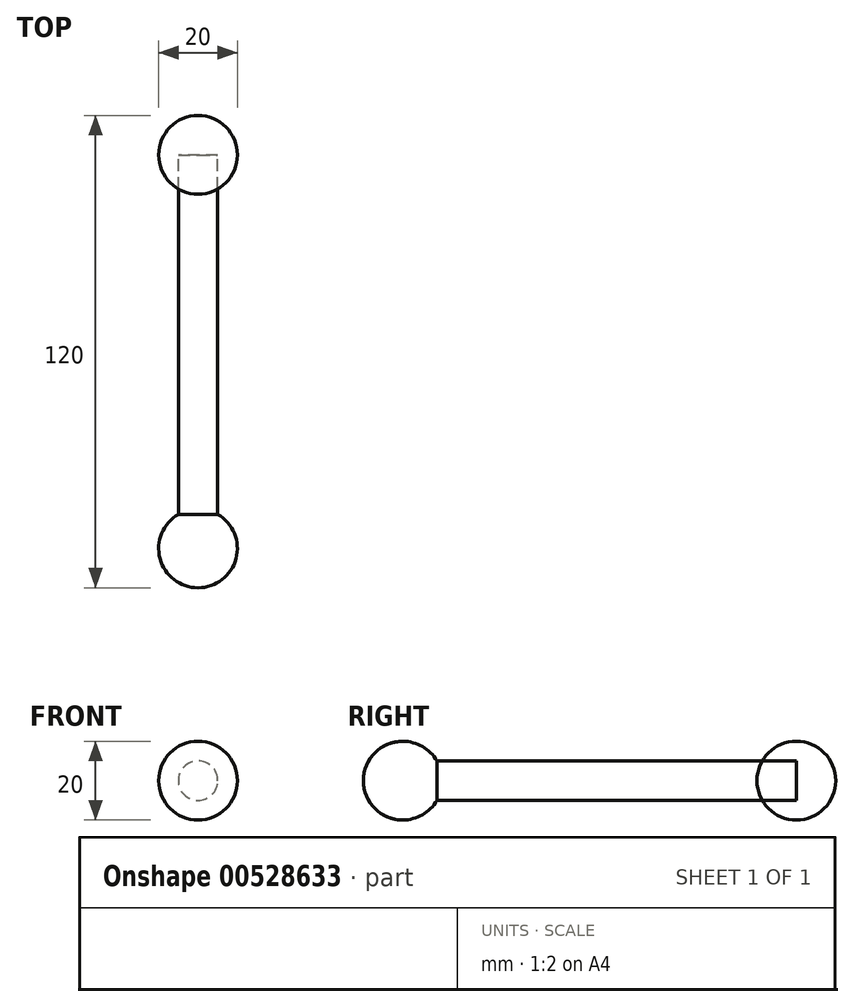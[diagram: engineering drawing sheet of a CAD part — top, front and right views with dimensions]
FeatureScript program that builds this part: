
annotation { "Feature Type Name" : "Feature", "Feature Type Description" : "" }
export const myFeature = defineFeature(function(context is Context, id is Id, definition is map)
    precondition{}
    {
        {
            var Q0;
            Q0=qCreatedBy(makeId("Front.planeOp"),FACE);
            var sketch = newSketch(context, id + "F0", { "sketchPlane" : qUnion([Q0])});
            skCircle(sketch, "E0", {"center": v(0, 0) * mm, "radius": 5 * mm});
            skSolve(sketch);
        }
        {
            var Q0;
            Q0 = qSketchRegion(id + "F0", true);
            extrude(context, id + "F1", {"entities" : qUnion([Q0]), "depth" : 100 * mm, "offsetDistance" : 25 * mm});
        }
        {
            var Q0;
            Q0=qCreatedBy(makeId("Right.planeOp"),FACE);
            var sketch = newSketch(context, id + "F2", { "sketchPlane" : qUnion([Q0])});
            skLineSegment(sketch, "E1", {"start": v(0, 10) * mm, "end": v(0, -10) * mm});
            skArc(sketch, "E2", {"start": v(0, 10) * mm, "mid": v(-10, 0) * mm, "end": v(0, -10) * mm});
            skLineSegment(sketch, "E3", {"start": v(-8.66, -5) * mm, "end": v(-91.34, -5) * mm});
            skLineSegment(sketch, "E4", {"start": v(-91.34, 5) * mm, "end": v(-8.66, 5) * mm});
            skLineSegment(sketch, "E5", {"start": v(-50, 5) * mm, "end": v(-50, -10) * mm, "construction": true});
            skArc(sketch, "E6.MirrorCS", {"start": v(-100, 10) * mm, "mid": v(-90, 0) * mm, "end": v(-100, -10) * mm});
            skLineSegment(sketch, "E7.MirrorCS", {"start": v(-100, 10) * mm, "end": v(-100, -10) * mm});
            skPoint(sketch, "E8.orphan", {"position": v(0, 5) * mm});
            skPoint(sketch, "E9.orphan", {"position": v(-100, 5) * mm});
            skSolve(sketch);
        }
        {
            var Q0;
            {var subQ0=sQuery(id+"F2.wireOp",EDGE,"E1");Q0=makeQuery(id+"F2.imprint","IMPRINT",FACE,{"disambiguationData":[TD([[makeQuery(id+"F2.imprint","IMPRINT",EDGE,{"derivedFrom":subQ0}),-1.0]])]});}
            var Q1;
            Q1=sQuery(id+"F2.wireOp",EDGE,"E1");
            revolve(context, id + "F3", {"entities" : qUnion([Q0]), "axis" : qUnion([Q1]), "revolveType" : RevolveType.FULL});
        }
        {
            var Q0;
            {var subQ2=sQuery(id+"F2.wireOp",EDGE,"E7.MirrorCS");Q0=makeQuery(id+"F2.imprint","IMPRINT",FACE,{"disambiguationData":[TD([[makeQuery(id+"F2.imprint","IMPRINT",EDGE,{"derivedFrom":subQ2}),1.0]])]});}
            var Q1;
            Q1=sQuery(id+"F2.wireOp",EDGE,"E7.MirrorCS");
            revolve(context, id + "F4", {"operationType" : NewBodyOperationType.ADD, "entities" : qUnion([Q0]), "axis" : qUnion([Q1]), "revolveType" : RevolveType.FULL});
        }
    });
